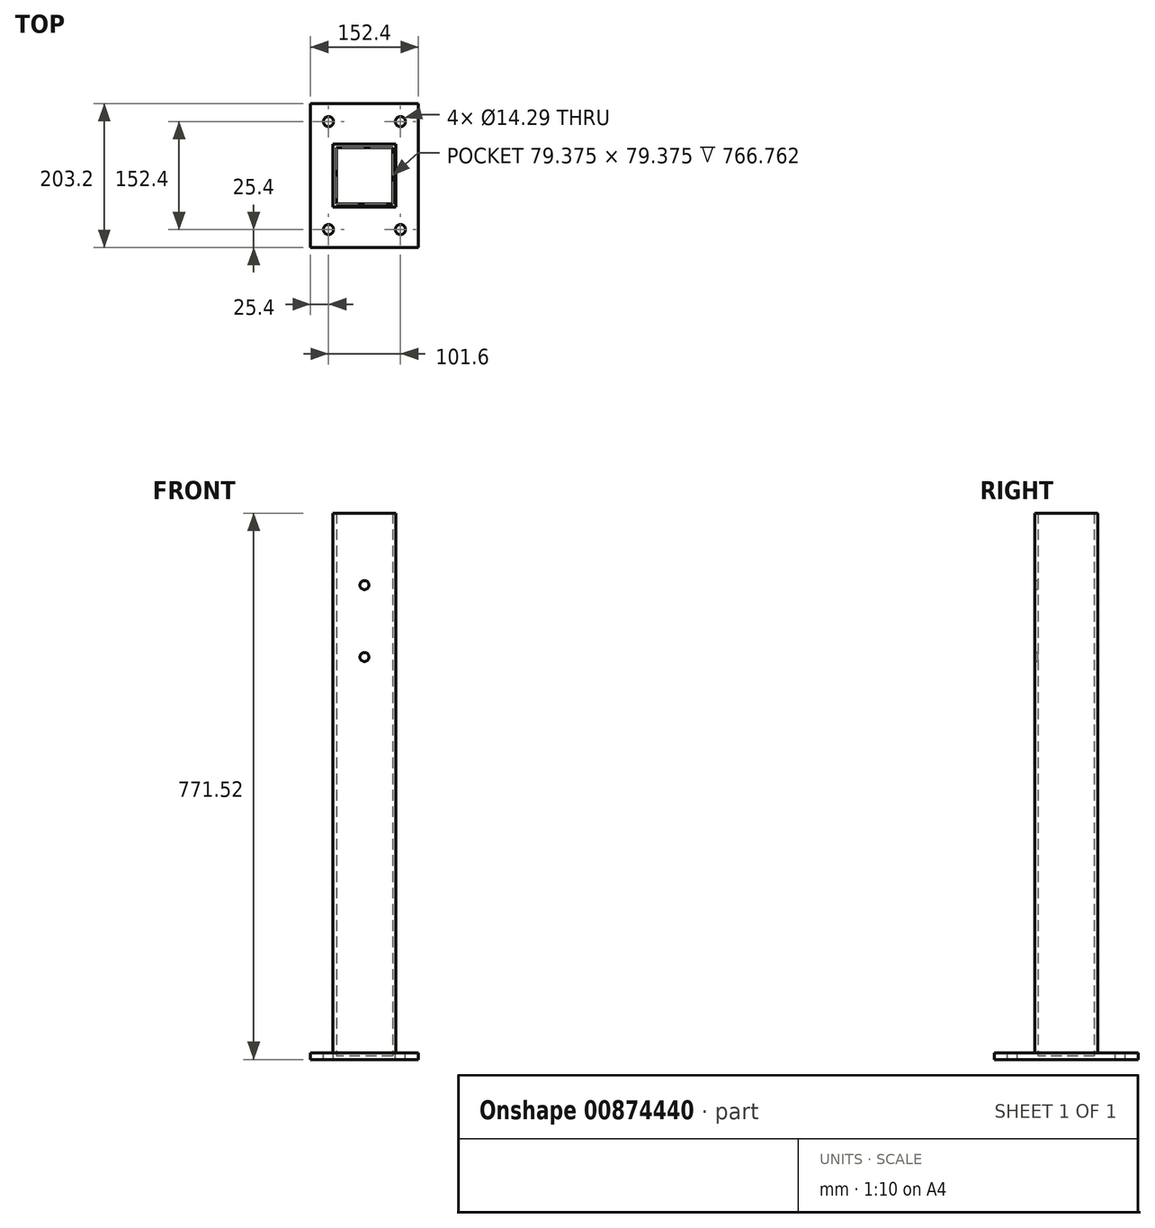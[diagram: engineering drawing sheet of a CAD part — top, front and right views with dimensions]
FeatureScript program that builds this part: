
annotation { "Feature Type Name" : "Feature", "Feature Type Description" : "" }
export const myFeature = defineFeature(function(context is Context, id is Id, definition is map)
    precondition{}
    {
        {
            var Q0;
            Q0=qCreatedBy(makeId("Top.planeOp"),FACE);
            var sketch = newSketch(context, id + "F0", { "sketchPlane" : qUnion([Q0])});
            skLineSegment(sketch, "E0.bottom", {"start": v(0, 0) * mm, "end": v(152.4, 0) * mm});
            skLineSegment(sketch, "E0.top", {"start": v(0, 203.2) * mm, "end": v(152.4, 203.2) * mm});
            skLineSegment(sketch, "E0.left", {"start": v(0, 0) * mm, "end": v(0, 203.2) * mm});
            skLineSegment(sketch, "E0.right", {"start": v(152.4, 0) * mm, "end": v(152.4, 203.2) * mm});
            skSolve(sketch);
        }
        {
            var Q0;
            Q0 = qSketchRegion(id + "F0", true);
            extrude(context, id + "F1", {"entities" : qUnion([Q0]), "depth" : 9.52 * mm, "offsetDistance" : 25.4 * mm});
        }
        {
            var Q0;
            Q0=makeQuery(id+"F1.opExtrude","CAP_FACE",FACE,{"disambiguationData":[OSD([sQuery(id+"F0.wireOp",EDGE,"E0.bottom"),sQuery(id+"F0.wireOp",EDGE,"E0.top"),sQuery(id+"F0.wireOp",EDGE,"E0.left"),sQuery(id+"F0.wireOp",EDGE,"E0.right")])],"isStart":false});
            var sketch = newSketch(context, id + "F2", { "sketchPlane" : qUnion([Q0])});
            skLineSegment(sketch, "E1.bottom", {"start": v(120.65, 146.05) * mm, "end": v(31.75, 146.05) * mm});
            skLineSegment(sketch, "E1.top", {"start": v(120.65, 57.15) * mm, "end": v(31.75, 57.15) * mm});
            skLineSegment(sketch, "E1.left", {"start": v(120.65, 146.05) * mm, "end": v(120.65, 57.15) * mm});
            skLineSegment(sketch, "E1.right", {"start": v(31.75, 146.05) * mm, "end": v(31.75, 57.15) * mm});
            skPoint(sketch, "E1.middle", {"position": v(76.2, 101.6) * mm});
            skSolve(sketch);
        }
        {
            var Q0;
            Q0 = qSketchRegion(id + "F2", true);
            extrude(context, id + "F3", {"entities" : qUnion([Q0]), "operationType" : NewBodyOperationType.ADD, "depth" : 762 * mm, "offsetDistance" : 25.4 * mm});
        }
        {
            var Q0;
            Q0=makeQuery(id+"F1.opExtrude","CAP_FACE",FACE,{"disambiguationData":[OSD([sQuery(id+"F0.wireOp",EDGE,"E0.bottom"),sQuery(id+"F0.wireOp",EDGE,"E0.top"),sQuery(id+"F0.wireOp",EDGE,"E0.left"),sQuery(id+"F0.wireOp",EDGE,"E0.right")])],"isStart":false});
            var sketch = newSketch(context, id + "F4", { "sketchPlane" : qUnion([Q0])});
            skCircle(sketch, "E2", {"center": v(127, 177.8) * mm, "radius": 7.14 * mm});
            skCircle(sketch, "E3", {"center": v(127, 25.4) * mm, "radius": 7.14 * mm});
            skCircle(sketch, "E4", {"center": v(25.4, 25.4) * mm, "radius": 7.14 * mm});
            skCircle(sketch, "E5", {"center": v(25.4, 177.8) * mm, "radius": 7.14 * mm});
            skSolve(sketch);
        }
        {
            var Q0;
            Q0 = qSketchRegion(id + "F4", true);
            extrude(context, id + "F5", {"entities" : qUnion([Q0]), "operationType" : NewBodyOperationType.REMOVE, "oppositeDirection" : true, "depth" : 25.4 * mm, "offsetDistance" : 25.4 * mm});
        }
        {
            var Q0;
            Q0=makeQuery(id+"F3.opExtrude","SWEPT_FACE",FACE,{"disambiguationData":[OSD([sQuery(id+"F2.wireOp",EDGE,"E1.top")])]});
            var sketch = newSketch(context, id + "F6", { "sketchPlane" : qUnion([Q0])});
            skCircle(sketch, "E6", {"center": v(76.2, 669.93) * mm, "radius": 6.35 * mm});
            skPoint(sketch, "E6.centerSnap0", {"position": v(76.2, 771.53) * mm});
            skCircle(sketch, "E7", {"center": v(76.2, 568.33) * mm, "radius": 6.35 * mm});
            skSolve(sketch);
        }
        {
            var Q0;
            Q0=makeQuery(id+"F3.opExtrude","CAP_FACE",FACE,{"disambiguationData":[OSD([sQuery(id+"F2.wireOp",EDGE,"E1.bottom"),sQuery(id+"F2.wireOp",EDGE,"E1.top"),sQuery(id+"F2.wireOp",EDGE,"E1.left"),sQuery(id+"F2.wireOp",EDGE,"E1.right")])],"isStart":false});
            shell(context, id + "F7", {"entities" : qUnion([Q0]), "thickness" : 4.76 * mm});
        }
        {
            var Q0;
            Q0 = qSketchRegion(id + "F6", true);
            extrude(context, id + "F8", {"entities" : qUnion([Q0]), "operationType" : NewBodyOperationType.REMOVE, "oppositeDirection" : true, "depth" : 25.4 * mm, "offsetDistance" : 25.4 * mm});
        }
    });
